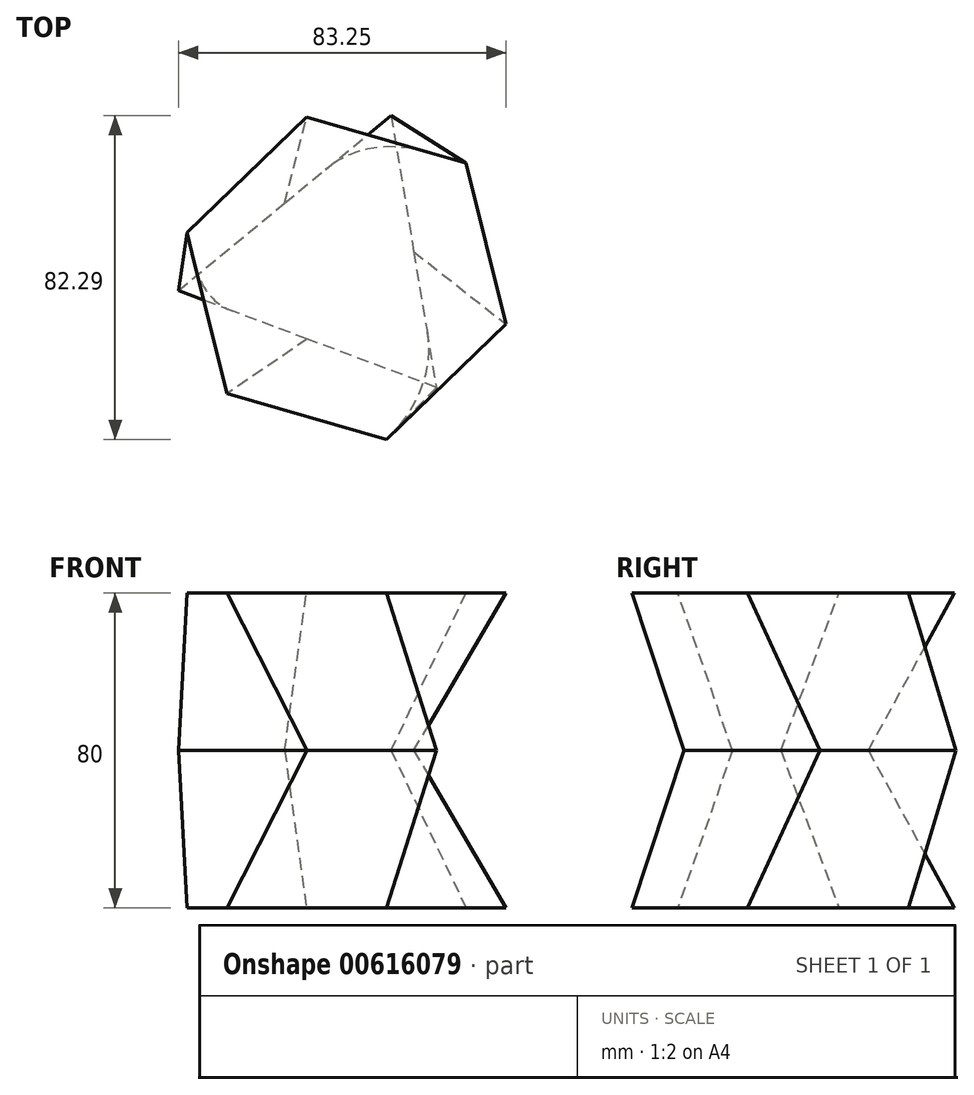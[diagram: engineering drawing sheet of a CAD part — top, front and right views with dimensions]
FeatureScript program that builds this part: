
annotation { "Feature Type Name" : "Feature", "Feature Type Description" : "" }
export const myFeature = defineFeature(function(context is Context, id is Id, definition is map)
    precondition{}
    {
        {
            var Q0;
            Q0=qCreatedBy(makeId("Top.planeOp"),FACE);
            var sketch = newSketch(context, id + "F0", { "sketchPlane" : qUnion([Q0])});
            skCircle(sketch, "E0.cCircle", {"center": v(0, 0) * mm, "radius": 36.54 * mm, "construction": true});
            skLineSegment(sketch, "E0.0", {"start": v(40.54, -11.66) * mm, "end": v(10.17, -40.94) * mm});
            skLineSegment(sketch, "E0.1", {"start": v(10.17, -40.94) * mm, "end": v(-30.37, -29.28) * mm});
            skLineSegment(sketch, "E0.2", {"start": v(-30.37, -29.28) * mm, "end": v(-40.54, 11.66) * mm});
            skLineSegment(sketch, "E0.3", {"start": v(-40.54, 11.66) * mm, "end": v(-10.17, 40.94) * mm});
            skLineSegment(sketch, "E0.4", {"start": v(-10.17, 40.94) * mm, "end": v(30.37, 29.28) * mm});
            skLineSegment(sketch, "E0.5", {"start": v(30.37, 29.28) * mm, "end": v(40.54, -11.66) * mm});
            skPoint(sketch, "E0.0.midPoint", {"position": v(25.36, -26.3) * mm});
            skSolve(sketch);
        }
        {
            var Q0;
            Q0=qCreatedBy(makeId("Top.planeOp"),FACE);
            cPlane(context, id + "F1", {"entities" : qUnion([Q0]), "cplaneType" : CPlaneType.OFFSET, "offset" : 40 * mm, "width" : 150 * mm, "height" : 150 * mm});
        }
        {
            var Q0;
            Q0=qCreatedBy(id+"F1.planeOp",FACE);
            var sketch = newSketch(context, id + "F2", { "sketchPlane" : qUnion([Q0])});
            skCircle(sketch, "E1.cCircle", {"center": v(-2.85, 3.5) * mm, "radius": 20.2 * mm, "construction": true});
            skLineSegment(sketch, "E1.0", {"start": v(22.83, -27.7) * mm, "end": v(-42.71, -3.13) * mm});
            skLineSegment(sketch, "E1.1", {"start": v(-42.71, -3.13) * mm, "end": v(11.34, 41.35) * mm});
            skLineSegment(sketch, "E1.2", {"start": v(11.34, 41.35) * mm, "end": v(22.83, -27.7) * mm});
            skPoint(sketch, "E1.0.midPoint", {"position": v(-9.94, -15.41) * mm});
            skSolve(sketch);
        }
        {
            var Q0;
            Q0 = qSketchRegion(id + "F2", true);
            var Q1;
            Q1 = qSketchRegion(id + "F0", true);
            loft(context, id + "F3", {"sheetProfilesArray" : [{ "sheetProfileEntities" : qUnion([Q0]) }, { "sheetProfileEntities" : qUnion([Q1]) }]});
        }
        {
            var Q0;
            Q0=makeQuery(id+"F3.opLoft","SWEPT_BODY",BODY,{"disambiguationData":[OSD([makeQuery(id+"F0.imprint","IMPRINT",FACE,{"disambiguationData":[TD([[makeQuery(id+"F0.imprint","IMPRINT",EDGE,{"derivedFrom":sQuery(id+"F0.wireOp",EDGE,"E0.0")}),-1.0]])]}),makeQuery(id+"F2.imprint","IMPRINT",FACE,{"disambiguationData":[TD([[makeQuery(id+"F2.imprint","IMPRINT",EDGE,{"derivedFrom":sQuery(id+"F2.wireOp",EDGE,"E1.0")}),-1.0]])]})])]});
            var Q1;
            Q1=qCreatedBy(id+"F1.planeOp",FACE);
            mirror(context, id + "F4", {"operationType" : NewBodyOperationType.ADD, "entities" : qUnion([Q0]), "mirrorPlane" : qUnion([Q1])});
        }
    });
